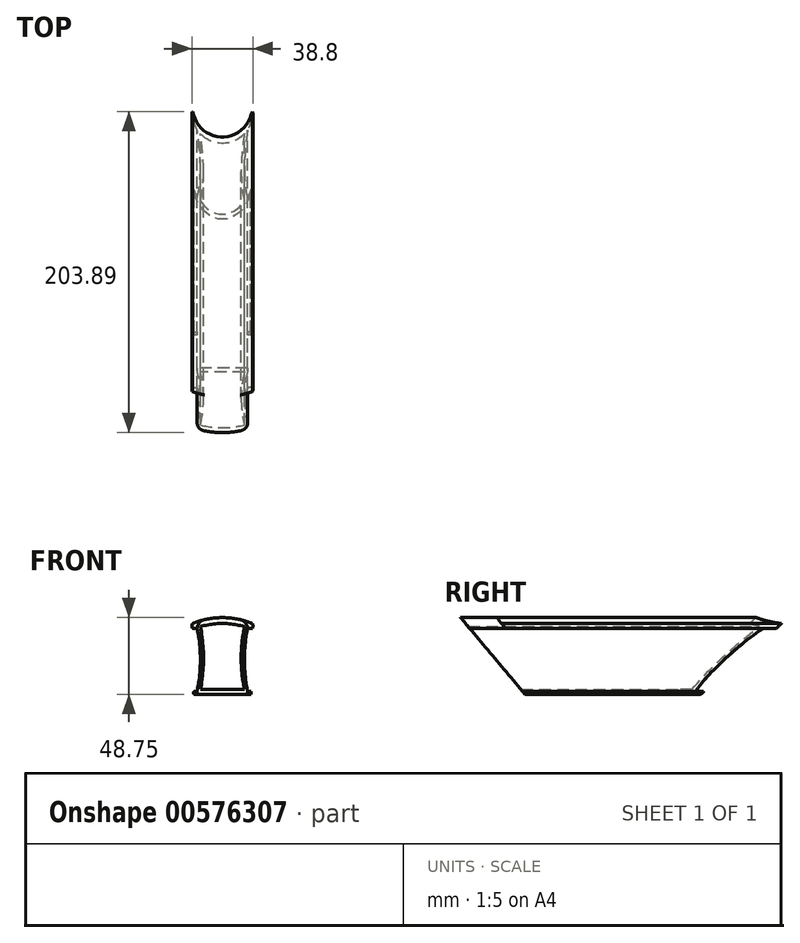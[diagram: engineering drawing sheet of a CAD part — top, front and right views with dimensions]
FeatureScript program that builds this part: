
annotation { "Feature Type Name" : "Feature", "Feature Type Description" : "" }
export const myFeature = defineFeature(function(context is Context, id is Id, definition is map)
    precondition{}
    {
        {
            var Q0;
            Q0=qCreatedBy(makeId("Front.planeOp"),FACE);
            var sketch = newSketch(context, id + "F0", { "sketchPlane" : qUnion([Q0])});
            skLineSegment(sketch, "E0", {"start": v(0, 0) * mm, "end": v(18, 0) * mm});
            skLineSegment(sketch, "E1", {"start": v(0, 0) * mm, "end": v(-18, 0) * mm});
            skLineSegment(sketch, "E2", {"start": v(-16, 42) * mm, "end": v(-19, 42) * mm});
            skArc(sketch, "E3", {"start": v(-19, 45) * mm, "mid": v(-19.4, 43.5) * mm, "end": v(-19, 42) * mm});
            skArc(sketch, "E4", {"start": v(19, 45) * mm, "mid": v(0, 48.75) * mm, "end": v(-19, 45) * mm});
            skArc(sketch, "E5", {"start": v(19, 42) * mm, "mid": v(19.4, 43.5) * mm, "end": v(19, 45) * mm});
            skLineSegment(sketch, "E6", {"start": v(19, 42) * mm, "end": v(16, 42) * mm});
            skLineSegment(sketch, "E7", {"start": v(18, 2) * mm, "end": v(16, 2) * mm});
            skArc(sketch, "E8", {"start": v(16, 42) * mm, "mid": v(13.98, 22) * mm, "end": v(16, 2) * mm});
            skLineSegment(sketch, "E9", {"start": v(-18, 2) * mm, "end": v(-16, 2) * mm});
            skArc(sketch, "E10", {"start": v(-16, 2) * mm, "mid": v(-13.98, 22) * mm, "end": v(-16, 42) * mm});
            skLineSegment(sketch, "E11", {"start": v(0, 3) * mm, "end": v(-14, 3) * mm});
            skLineSegment(sketch, "E12", {"start": v(0, 3) * mm, "end": v(14, 3) * mm});
            skArc(sketch, "E13", {"start": v(-14, 3) * mm, "mid": v(-11.98, 23) * mm, "end": v(-14, 43) * mm});
            skArc(sketch, "E14", {"start": v(14, 43) * mm, "mid": v(11.98, 23) * mm, "end": v(14, 3) * mm});
            skArc(sketch, "E15", {"start": v(14, 43) * mm, "mid": v(0, 45) * mm, "end": v(-14, 43) * mm});
            skArc(sketch, "E16", {"start": v(-18, 2) * mm, "mid": v(-18.27, 1) * mm, "end": v(-18, 0) * mm});
            skArc(sketch, "E17", {"start": v(18, 0) * mm, "mid": v(18.27, 1) * mm, "end": v(18, 2) * mm});
            skSolve(sketch);
        }
        {
            var Q0;
            Q0 = qSketchRegion(id + "F0", true);
            extrude(context, id + "F1", {"entities" : qUnion([Q0]), "depth" : 207.98 * mm, "offsetDistance" : 25 * mm});
        }
        {
            var Q0;
            Q0=makeQuery(id+"F1.opExtrude","CAP_EDGE",EDGE,{"disambiguationData":[OSD([sQuery(id+"F0.wireOp",EDGE,"E0"),sQuery(id+"F0.wireOp",EDGE,"E1")])],"isStart":false});
            chamfer(context, id + "F2", {"entities" : qUnion([Q0]), "chamferType" : ChamferType.OFFSET_ANGLE, "width" : 45 * mm, "oppositeDirection" : false, "angle" : 50 * degree, "tangentPropagation" : true});
        }
        {
            var Q0;
            Q0=makeQuery(id+"F1.opExtrude","CAP_EDGE",EDGE,{"disambiguationData":[OSD([sQuery(id+"F0.wireOp",EDGE,"E0"),sQuery(id+"F0.wireOp",EDGE,"E1")])],"isStart":true});
            chamfer(context, id + "F3", {"entities" : qUnion([Q0]), "chamferType" : ChamferType.OFFSET_ANGLE, "width" : 45 * mm, "oppositeDirection" : false, "angle" : 47 * degree, "tangentPropagation" : true});
        }
        {
            var Q0;
            Q0=makeQuery(id+"F1.opExtrude","SWEPT_FACE",FACE,{"disambiguationData":[OSD([sQuery(id+"F0.wireOp",EDGE,"E11"),sQuery(id+"F0.wireOp",EDGE,"E12")])]});
            var Q1;
            Q1=makeQuery(id+"F1.opExtrude","SWEPT_EDGE",EDGE,{"disambiguationData":[OSD([sQuery(id+"F0.wireOp",EDGE,"E12"),sQuery(id+"F0.wireOp",EDGE,"E14")])]});
            cPlane(context, id + "F4", {"entities" : qUnion([Q0, Q1]), "cplaneType" : CPlaneType.LINE_ANGLE, "offset" : 25 * mm, "angle" : 90 * degree, "width" : 150 * mm, "height" : 150 * mm});
        }
        {
            var Q0;
            Q0=qCreatedBy(id+"F4.planeOp",FACE);
            var sketch = newSketch(context, id + "F5", { "sketchPlane" : qUnion([Q0])});
            skLineSegment(sketch, "E18", {"start": v(140.14, 0) * mm, "end": v(200.72, 72.2) * mm});
            skLineSegment(sketch, "E19", {"start": v(200.72, 72.2) * mm, "end": v(232.27, 72.2) * mm});
            skLineSegment(sketch, "E20", {"start": v(232.27, 72.2) * mm, "end": v(198.05, 0) * mm});
            skLineSegment(sketch, "E21", {"start": v(198.05, 0) * mm, "end": v(140.14, 0) * mm});
            skSolve(sketch);
        }
        {
            var Q0;
            Q0=makeQuery(id+"F5.imprint","IMPRINT",FACE,{"disambiguationData":[TD([[makeQuery(id+"F5.imprint","IMPRINT",EDGE,{"derivedFrom":sQuery(id+"F5.wireOp",EDGE,"E18")}),-1.0]])]});
            extrude(context, id + "F6", {"entities" : qUnion([Q0]), "operationType" : NewBodyOperationType.REMOVE, "oppositeDirection" : true, "depth" : 6 * mm, "offsetDistance" : 25 * mm, "hasSecondDirection" : true, "secondDirectionOppositeDirection" : true, "secondDirectionDepth" : 2 * mm});
        }
        {
            var Q0;
            Q0=makeQuery(id+"F1.opExtrude","SWEPT_FACE",FACE,{"disambiguationData":[OSD([sQuery(id+"F0.wireOp",EDGE,"E11"),sQuery(id+"F0.wireOp",EDGE,"E12")])]});
            var Q1;
            Q1=makeQuery(id+"F1.opExtrude","SWEPT_EDGE",EDGE,{"disambiguationData":[OSD([sQuery(id+"F0.wireOp",EDGE,"E11"),sQuery(id+"F0.wireOp",EDGE,"E13")])]});
            cPlane(context, id + "F7", {"entities" : qUnion([Q0, Q1]), "cplaneType" : CPlaneType.LINE_ANGLE, "offset" : 25 * mm, "angle" : 90 * degree, "width" : 150 * mm, "height" : 150 * mm});
        }
        {
            var Q0;
            Q0=qCreatedBy(id+"F7.planeOp",FACE);
            var sketch = newSketch(context, id + "F8", { "sketchPlane" : qUnion([Q0])});
            skLineSegment(sketch, "E22", {"start": v(140.14, 0) * mm, "end": v(185.93, 54.57) * mm});
            skLineSegment(sketch, "E23", {"start": v(185.93, 54.57) * mm, "end": v(210.62, 54.57) * mm});
            skLineSegment(sketch, "E24", {"start": v(210.62, 54.57) * mm, "end": v(168.94, 0) * mm});
            skLineSegment(sketch, "E25", {"start": v(168.94, 0) * mm, "end": v(140.14, 0) * mm});
            skSolve(sketch);
        }
        {
            var Q0;
            Q0=makeQuery(id+"F8.imprint","IMPRINT",FACE,{"disambiguationData":[TD([[makeQuery(id+"F8.imprint","IMPRINT",EDGE,{"derivedFrom":sQuery(id+"F8.wireOp",EDGE,"E22")}),-1.0]])]});
            extrude(context, id + "F9", {"entities" : qUnion([Q0]), "operationType" : NewBodyOperationType.REMOVE, "depth" : 6 * mm, "offsetDistance" : 25 * mm, "hasSecondDirection" : true, "secondDirectionOppositeDirection" : false, "secondDirectionDepth" : 2 * mm});
        }
        {
            var Q0;
            Q0=makeQuery(id+"F3.opChamfer","BLEND_FACE",FACE,{"disambiguationData":[OSD([sQuery(id+"F0.wireOp",EDGE,"E0"),sQuery(id+"F0.wireOp",EDGE,"E1")])]});
            var Q1;
            {var subQ0=sQuery(id+"F0.wireOp",EDGE,"E1");var subQ1=sQuery(id+"F0.wireOp",EDGE,"E0");Q1=makeQuery(id+"F3.opChamfer","BLEND_EDGE",EDGE,{"disambiguationData":[OD(1.0)],"blendedFrom":[makeQuery(id+"F1.opExtrude","CAP_EDGE",EDGE,{"disambiguationData":[OSD([subQ1,subQ0])],"isStart":true}),makeQuery(id+"F1.opExtrude","CAP_FACE",FACE,{"disambiguationData":[OSD([subQ1,subQ0,sQuery(id+"F0.wireOp",EDGE,"E2"),sQuery(id+"F0.wireOp",EDGE,"E3"),sQuery(id+"F0.wireOp",EDGE,"E4"),sQuery(id+"F0.wireOp",EDGE,"E5"),sQuery(id+"F0.wireOp",EDGE,"E6"),sQuery(id+"F0.wireOp",EDGE,"E7"),sQuery(id+"F0.wireOp",EDGE,"E8"),sQuery(id+"F0.wireOp",EDGE,"E9"),sQuery(id+"F0.wireOp",EDGE,"E10"),sQuery(id+"F0.wireOp",EDGE,"E11"),sQuery(id+"F0.wireOp",EDGE,"E12"),sQuery(id+"F0.wireOp",EDGE,"E13"),sQuery(id+"F0.wireOp",EDGE,"E14"),sQuery(id+"F0.wireOp",EDGE,"E15"),sQuery(id+"F0.wireOp",EDGE,"E16"),sQuery(id+"F0.wireOp",EDGE,"E17")])],"isStart":true})],"blendedInto":[makeQuery(id+"F1.opExtrude","CAP_FACE",FACE,{"disambiguationData":[OSD([subQ1,subQ0,sQuery(id+"F0.wireOp",EDGE,"E2"),sQuery(id+"F0.wireOp",EDGE,"E3"),sQuery(id+"F0.wireOp",EDGE,"E4"),sQuery(id+"F0.wireOp",EDGE,"E5"),sQuery(id+"F0.wireOp",EDGE,"E6"),sQuery(id+"F0.wireOp",EDGE,"E7"),sQuery(id+"F0.wireOp",EDGE,"E8"),sQuery(id+"F0.wireOp",EDGE,"E9"),sQuery(id+"F0.wireOp",EDGE,"E10"),sQuery(id+"F0.wireOp",EDGE,"E11"),sQuery(id+"F0.wireOp",EDGE,"E12"),sQuery(id+"F0.wireOp",EDGE,"E13"),sQuery(id+"F0.wireOp",EDGE,"E14"),sQuery(id+"F0.wireOp",EDGE,"E15"),sQuery(id+"F0.wireOp",EDGE,"E16"),sQuery(id+"F0.wireOp",EDGE,"E17")])],"isStart":true})]});}
            cPlane(context, id + "F10", {"entities" : qUnion([Q0, Q1]), "cplaneType" : CPlaneType.LINE_ANGLE, "offset" : 25 * mm, "angle" : 90 * degree, "width" : 150 * mm, "height" : 150 * mm});
        }
        {
            var Q0;
            Q0=qCreatedBy(id+"F10.planeOp",FACE);
            var sketch = newSketch(context, id + "F11", { "sketchPlane" : qUnion([Q0])});
            skCircle(sketch, "E26", {"center": v(0, 26.67) * mm, "radius": 20 * mm});
            skSolve(sketch);
        }
        {
            var Q0;
            Q0=makeQuery(id+"F11.imprint","IMPRINT",FACE,{"disambiguationData":[TD([[makeQuery(id+"F11.imprint","IMPRINT",EDGE,{"derivedFrom":sQuery(id+"F11.wireOp",EDGE,"E26")}),1.0]])]});
            extrude(context, id + "F12", {"entities" : qUnion([Q0]), "operationType" : NewBodyOperationType.REMOVE, "oppositeDirection" : true, "depth" : 90 * mm, "offsetDistance" : 25 * mm, "hasSecondDirection" : true, "secondDirectionOppositeDirection" : false, "secondDirectionDepth" : 5 * mm});
        }
        {
            var Q0;
            Q0=makeQuery(id+"F6.boolean.opBoolean","INTERSECT",EDGE,{"derivedFrom":[makeQuery(id+"F1.opExtrude","SWEPT_FACE",FACE,{"disambiguationData":[OSD([sQuery(id+"F0.wireOp",EDGE,"E4")])]}),makeQuery(id+"F6.opExtrude","CAP_FACE",FACE,{"disambiguationData":[OSD([sQuery(id+"F5.wireOp",EDGE,"E18"),sQuery(id+"F5.wireOp",EDGE,"E19"),sQuery(id+"F5.wireOp",EDGE,"E20"),sQuery(id+"F5.wireOp",EDGE,"E21")])],"isStart":true})]});
            var Q1;
            Q1=makeQuery(id+"F9.boolean.opBoolean","INTERSECT",EDGE,{"derivedFrom":[makeQuery(id+"F1.opExtrude","SWEPT_FACE",FACE,{"disambiguationData":[OSD([sQuery(id+"F0.wireOp",EDGE,"E4")])]}),makeQuery(id+"F9.opExtrude","CAP_FACE",FACE,{"disambiguationData":[OSD([sQuery(id+"F8.wireOp",EDGE,"E22"),sQuery(id+"F8.wireOp",EDGE,"E23"),sQuery(id+"F8.wireOp",EDGE,"E24"),sQuery(id+"F8.wireOp",EDGE,"E25")])],"isStart":true})]});
            fillet(context, id + "F13", {"entities" : qUnion([Q0, Q1]), "radius" : 6 * mm, "tangentPropagation" : true, "allowEdgeOverflow" : false});
        }
    });
